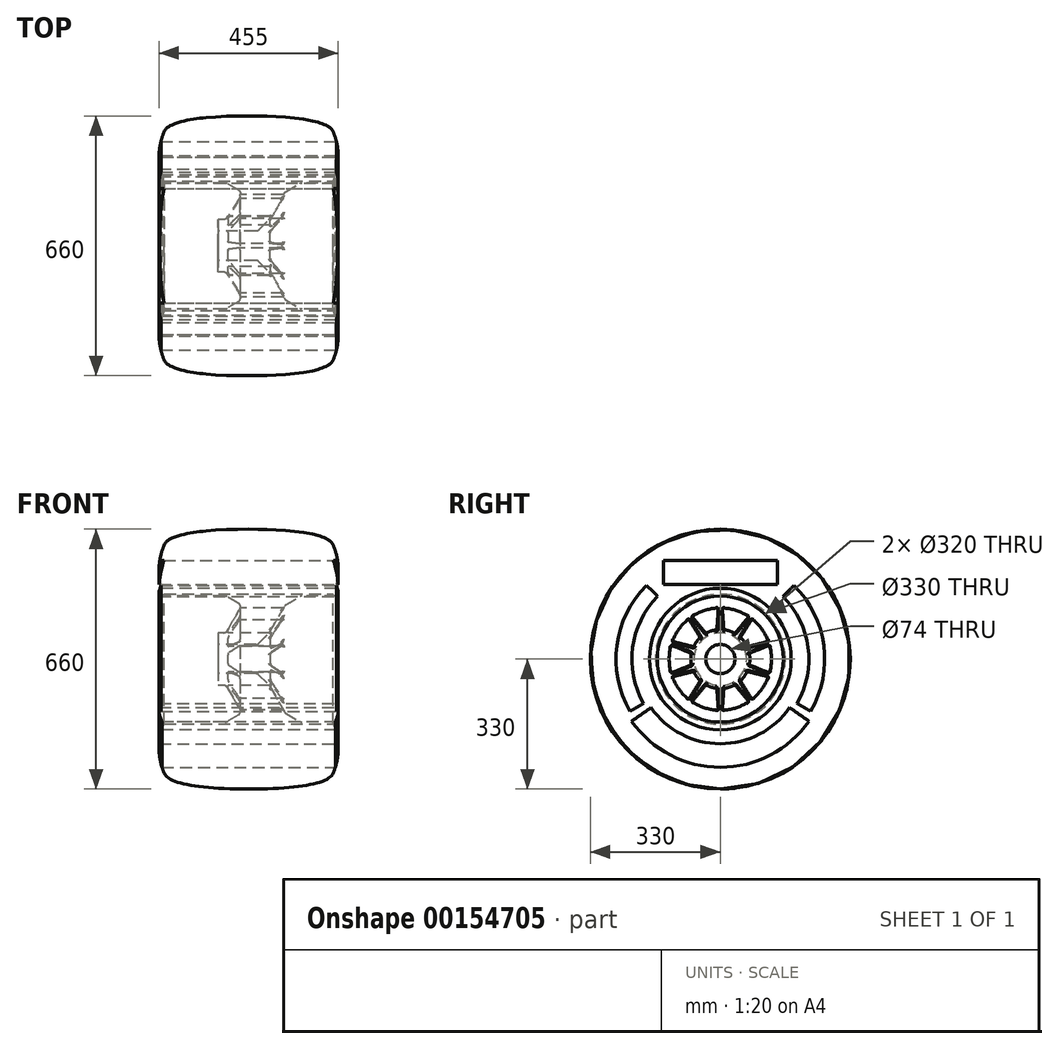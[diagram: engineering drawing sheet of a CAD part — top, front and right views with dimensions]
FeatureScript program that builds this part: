
annotation { "Feature Type Name" : "Feature", "Feature Type Description" : "" }
export const myFeature = defineFeature(function(context is Context, id is Id, definition is map)
    precondition{}
    {
        {
            var Q0;
            Q0=qCreatedBy(makeId("Front.planeOp"),FACE);
            var sketch = newSketch(context, id + "F0", { "sketchPlane" : qUnion([Q0])});
            skLineSegment(sketch, "E0.bottom", {"start": v(0, 0) * mm, "end": v(-232.5, 0) * mm, "construction": true});
            skLineSegment(sketch, "E0.top", {"start": v(0, 340) * mm, "end": v(-232.5, 340) * mm, "construction": true});
            skLineSegment(sketch, "E0.left", {"start": v(0, 0) * mm, "end": v(0, 340) * mm, "construction": true});
            skLineSegment(sketch, "E0.right", {"start": v(-232.5, 0) * mm, "end": v(-232.5, 340) * mm, "construction": true});
            skLineSegment(sketch, "E1", {"start": v(0, 165) * mm, "end": v(-214.65, 165) * mm});
            skEllipticalArc(sketch, "E2", {});
            skLineSegment(sketch, "E3", {"start": v(0, 330) * mm, "end": v(-232.5, 330) * mm, "construction": true});
            skLineSegment(sketch, "E4", {"start": v(-214.65, 165) * mm, "end": v(-214.65, 290) * mm, "construction": true});
            skEllipticalArc(sketch, "E5", {});
            skLineSegment(sketch, "E6", {"start": v(-227.5, 227.5) * mm, "end": v(-214.65, 227.5) * mm, "construction": true});
            skLineSegment(sketch, "E7.MirrorCS", {"start": v(0, 165) * mm, "end": v(214.65, 165) * mm});
            skEllipticalArc(sketch, "E8.MirrorCS", {});
            skEllipticalArc(sketch, "E9.MirrorCS", {});
            skLineSegment(sketch, "E10", {"start": v(-227.5, 227.5) * mm, "end": v(-227.5, 0) * mm, "construction": true});
            skLineSegment(sketch, "E11.MirrorCS", {"start": v(232.5, 0) * mm, "end": v(232.5, 340) * mm, "construction": true});
            skLineSegment(sketch, "E12.MirrorCS", {"start": v(0, 340) * mm, "end": v(232.5, 340) * mm, "construction": true});
            skLineSegment(sketch, "E13.MirrorCS", {"start": v(0, 0) * mm, "end": v(232.5, 0) * mm, "construction": true});
            const initialGuessF0  = {"E2": [0.9663548736200733, 0.07278752318222956, 0.9840924206940259, -0.17765727548449584, 1.201246100909484, 0.14589798289999634, 2.549372753708736, 3.1145633278998273], "E5": [0.08535, 0.2275, -1, 0, 0.31285, 0.22033704343395144, 5.995580380133269, 0.28760492704630874], "E8.MirrorCS": [-0.08535, 0.2275, 1, 0, 0.31285, 0.22033704343395144, 5.995580380133277, 0.28760492704631696], "E9.MirrorCS": [-0.9663548736200733, 0.07278752318222961, -0.984092420694026, -0.17765727548449584, 1.201246100909484, 0.14589798289999634, 3.168621979279758, 3.733812553470848]};
            skSetInitialGuess(sketch, initialGuessF0);
            skSolve(sketch);
        }
        {
            var Q0;
            Q0=qCreatedBy(makeId("Right.planeOp"),FACE);
            var sketch = newSketch(context, id + "F1", { "sketchPlane" : qUnion([Q0])});
            skLineSegment(sketch, "E14", {"start": v(0, 190) * mm, "end": v(0, -215) * mm, "construction": true});
            skLineSegment(sketch, "E15.bottom", {"start": v(0, 190) * mm, "end": v(-145, 190) * mm});
            skLineSegment(sketch, "E15.top", {"start": v(0, 250) * mm, "end": v(-145, 250) * mm});
            skLineSegment(sketch, "E15.left", {"start": v(0, 190) * mm, "end": v(0, 250) * mm});
            skLineSegment(sketch, "E15.right", {"start": v(-145, 190) * mm, "end": v(-145, 250) * mm});
            skArc(sketch, "E16", {"start": v(-159.1, 159.1) * mm, "mid": v(-223.08, 29.37) * mm, "end": v(-194.86, -112.5) * mm});
            skArc(sketch, "E17", {"start": v(-187.38, 187.38) * mm, "mid": v(-262.73, 34.59) * mm, "end": v(-229.5, -132.5) * mm});
            skLineSegment(sketch, "E18", {"start": v(-159.1, 159.1) * mm, "end": v(-187.38, 187.38) * mm});
            skLineSegment(sketch, "E19", {"start": v(-194.86, -112.5) * mm, "end": v(-229.5, -132.5) * mm});
            skArc(sketch, "E20", {"start": v(-176.12, -123.32) * mm, "mid": v(-99.28, -190.7) * mm, "end": v(0, -215) * mm});
            skArc(sketch, "E21", {"start": v(-225.27, -157.73) * mm, "mid": v(-126.98, -243.93) * mm, "end": v(0, -275) * mm});
            skLineSegment(sketch, "E22", {"start": v(-176.12, -123.32) * mm, "end": v(-225.27, -157.73) * mm});
            skLineSegment(sketch, "E23", {"start": v(0, -215) * mm, "end": v(0, -275) * mm});
            skLineSegment(sketch, "E24.MirrorCS", {"start": v(0, 250) * mm, "end": v(145, 250) * mm});
            skLineSegment(sketch, "E25.MirrorCS", {"start": v(145, 190) * mm, "end": v(145, 250) * mm});
            skLineSegment(sketch, "E26.MirrorCS", {"start": v(0, 190) * mm, "end": v(145, 190) * mm});
            skLineSegment(sketch, "E27.MirrorCS", {"start": v(159.1, 159.1) * mm, "end": v(187.38, 187.38) * mm});
            skArc(sketch, "E28.MirrorCS", {"start": v(187.38, 187.38) * mm, "mid": v(262.73, 34.59) * mm, "end": v(229.5, -132.5) * mm});
            skArc(sketch, "E29.MirrorCS", {"start": v(159.1, 159.1) * mm, "mid": v(223.08, 29.37) * mm, "end": v(194.86, -112.5) * mm});
            skLineSegment(sketch, "E30.MirrorCS", {"start": v(194.86, -112.5) * mm, "end": v(229.5, -132.5) * mm});
            skLineSegment(sketch, "E31.MirrorCS", {"start": v(176.12, -123.32) * mm, "end": v(225.27, -157.73) * mm});
            skArc(sketch, "E32.MirrorCS", {"start": v(225.27, -157.73) * mm, "mid": v(126.98, -243.93) * mm, "end": v(0, -275) * mm});
            skArc(sketch, "E33.MirrorCS", {"start": v(176.12, -123.32) * mm, "mid": v(99.28, -190.7) * mm, "end": v(0, -215) * mm});
            skSolve(sketch);
        }
        {
            var Q0;
            Q0=qCreatedBy(makeId("Front.planeOp"),FACE);
            var sketch = newSketch(context, id + "F2", { "sketchPlane" : qUnion([Q0])});
            skLineSegment(sketch, "E34.bottom", {"start": v(-222.5, 180) * mm, "end": v(222.5, 180) * mm});
            skLineSegment(sketch, "E34.top", {"start": v(-222.5, 160) * mm, "end": v(-60.18, 160) * mm});
            skLineSegment(sketch, "E34.left", {"start": v(-227.5, 175) * mm, "end": v(-227.5, 165) * mm});
            skLineSegment(sketch, "E34.right", {"start": v(227.5, 175) * mm, "end": v(227.5, 165) * mm});
            skPoint(sketch, "E35.visualSharp", {"position": v(-227.5, 160) * mm});
            skArc(sketch, "E35.filletArc", {"start": v(-227.5, 165) * mm, "mid": v(-226.04, 161.46) * mm, "end": v(-222.5, 160) * mm});
            skPoint(sketch, "E36.visualSharp", {"position": v(227.5, 160) * mm});
            skArc(sketch, "E36.filletArc", {"start": v(222.5, 160) * mm, "mid": v(226.04, 161.46) * mm, "end": v(227.5, 165) * mm});
            skPoint(sketch, "E37.visualSharp", {"position": v(227.5, 180) * mm});
            skArc(sketch, "E37.filletArc", {"start": v(227.5, 175) * mm, "mid": v(226.04, 178.54) * mm, "end": v(222.5, 180) * mm});
            skPoint(sketch, "E38.visualSharp", {"position": v(-227.5, 180) * mm});
            skArc(sketch, "E38.filletArc", {"start": v(-222.5, 180) * mm, "mid": v(-226.04, 178.54) * mm, "end": v(-227.5, 175) * mm});
            skLineSegment(sketch, "E39", {"start": v(18.36, 37) * mm, "end": v(-77.5, 37) * mm});
            skLineSegment(sketch, "E40", {"start": v(-77.5, 37) * mm, "end": v(-77.5, 67) * mm});
            skLineSegment(sketch, "E41", {"start": v(-77.5, 67) * mm, "end": v(-63.27, 67) * mm});
            skLineSegment(sketch, "E42", {"start": v(-54.61, 72) * mm, "end": v(-22.23, 128.09) * mm});
            skLineSegment(sketch, "E43", {"start": v(-25.9, 141.75) * mm, "end": v(-55.18, 158.66) * mm});
            skLineSegment(sketch, "E44", {"start": v(25.43, 39.93) * mm, "end": v(51.57, 66.07) * mm});
            skLineSegment(sketch, "E45", {"start": v(53.16, 68.14) * mm, "end": v(91.43, 134.43) * mm});
            skLineSegment(sketch, "E46", {"start": v(95.1, 138.09) * mm, "end": v(130.72, 158.66) * mm});
            skLineSegment(sketch, "E47.trimOffspring", {"start": v(135.72, 160) * mm, "end": v(222.5, 160) * mm});
            skPoint(sketch, "E48.visualSharp", {"position": v(-57.5, 160) * mm});
            skArc(sketch, "E48.filletArc", {"start": v(-55.18, 158.66) * mm, "mid": v(-57.6, 159.66) * mm, "end": v(-60.18, 160) * mm});
            skPoint(sketch, "E49.visualSharp", {"position": v(-57.5, 67) * mm});
            skArc(sketch, "E49.filletArc", {"start": v(-63.27, 67) * mm, "mid": v(-58.27, 68.34) * mm, "end": v(-54.61, 72) * mm});
            skPoint(sketch, "E50.visualSharp", {"position": v(22.5, 37) * mm});
            skArc(sketch, "E50.filletArc", {"start": v(18.36, 37) * mm, "mid": v(22.18, 37.76) * mm, "end": v(25.43, 39.93) * mm});
            skPoint(sketch, "E51.visualSharp", {"position": v(52.5, 67) * mm});
            skArc(sketch, "E51.filletArc", {"start": v(51.57, 66.07) * mm, "mid": v(52.43, 67.05) * mm, "end": v(53.16, 68.14) * mm});
            skPoint(sketch, "E52.visualSharp", {"position": v(92.77, 136.75) * mm});
            skPoint(sketch, "E53.visualSharp", {"position": v(133.04, 160) * mm});
            skArc(sketch, "E53.filletArc", {"start": v(135.72, 160) * mm, "mid": v(133.13, 159.66) * mm, "end": v(130.72, 158.66) * mm});
            skPoint(sketch, "E54.visualSharp", {"position": v(-17.23, 136.75) * mm});
            skArc(sketch, "E54.filletArc", {"start": v(-22.23, 128.09) * mm, "mid": v(-21.23, 135.68) * mm, "end": v(-25.9, 141.75) * mm});
            skArc(sketch, "E55.filletArc", {"start": v(95.1, 138.09) * mm, "mid": v(93.02, 136.5) * mm, "end": v(91.43, 134.43) * mm});
            skSolve(sketch);
        }
        {
            var Q0;
            Q0=qCreatedBy(makeId("Right.planeOp"),FACE);
            var sketch = newSketch(context, id + "F3", { "sketchPlane" : qUnion([Q0])});
            skLineSegment(sketch, "E56", {"start": v(5.4, 124.22) * mm, "end": v(8.6, 78.49) * mm});
            skLineSegment(sketch, "E57", {"start": v(40.17, 123.64) * mm, "end": v(23.18, 71.33) * mm, "construction": true});
            skLineSegment(sketch, "E58", {"start": v(23.18, 71.33) * mm, "end": v(0, 0) * mm, "construction": true});
            skArc(sketch, "E59", {"start": v(23.18, 71.33) * mm, "mid": v(18, 72.8) * mm, "end": v(12.73, 73.91) * mm});
            skArc(sketch, "E60", {"start": v(40.17, 123.64) * mm, "mid": v(25.66, 127.44) * mm, "end": v(10.8, 129.55) * mm});
            skArc(sketch, "E61.MirrorCS", {"start": v(23.18, 71.33) * mm, "mid": v(28.23, 69.48) * mm, "end": v(33.14, 67.28) * mm});
            skLineSegment(sketch, "E62.MirrorCS", {"start": v(68.65, 103.67) * mm, "end": v(39.18, 68.55) * mm});
            skArc(sketch, "E63.MirrorCS", {"start": v(40.17, 123.64) * mm, "mid": v(54.15, 118.18) * mm, "end": v(67.4, 111.16) * mm});
            skPoint(sketch, "E64.visualSharp", {"position": v(8.88, 74.47) * mm});
            skArc(sketch, "E64.filletArc", {"start": v(8.6, 78.49) * mm, "mid": v(9.87, 75.49) * mm, "end": v(12.73, 73.91) * mm});
            skPoint(sketch, "E65.visualSharp", {"position": v(5, 129.9) * mm});
            skArc(sketch, "E65.filletArc", {"start": v(10.8, 129.55) * mm, "mid": v(6.87, 128.13) * mm, "end": v(5.4, 124.22) * mm});
            skPoint(sketch, "E66.visualSharp", {"position": v(36.6, 65.47) * mm});
            skArc(sketch, "E66.filletArc", {"start": v(33.14, 67.28) * mm, "mid": v(36.38, 66.87) * mm, "end": v(39.18, 68.55) * mm});
            skPoint(sketch, "E67.visualSharp", {"position": v(72.31, 108.03) * mm});
            skArc(sketch, "E67.filletArc", {"start": v(68.65, 103.67) * mm, "mid": v(69.75, 107.7) * mm, "end": v(67.4, 111.16) * mm});
            skLineSegment(sketch, "E68.1.0", {"start": v(-5.4, 124.22) * mm, "end": v(-8.6, 78.49) * mm});
            skArc(sketch, "E68.1.1", {"start": v(-5.4, 124.22) * mm, "mid": v(-6.87, 128.13) * mm, "end": v(-10.8, 129.55) * mm});
            skArc(sketch, "E68.1.2", {"start": v(-40.17, 123.64) * mm, "mid": v(-25.66, 127.44) * mm, "end": v(-10.8, 129.55) * mm});
            skArc(sketch, "E68.1.3", {"start": v(-40.17, 123.64) * mm, "mid": v(-54.15, 118.18) * mm, "end": v(-67.4, 111.16) * mm});
            skArc(sketch, "E68.1.4", {"start": v(-67.4, 111.16) * mm, "mid": v(-69.75, 107.7) * mm, "end": v(-68.65, 103.67) * mm});
            skLineSegment(sketch, "E68.1.5", {"start": v(-68.65, 103.67) * mm, "end": v(-39.18, 68.55) * mm});
            skArc(sketch, "E68.1.6", {"start": v(-39.18, 68.55) * mm, "mid": v(-36.38, 66.87) * mm, "end": v(-33.14, 67.28) * mm});
            skArc(sketch, "E68.1.7", {"start": v(-23.18, 71.33) * mm, "mid": v(-28.23, 69.48) * mm, "end": v(-33.14, 67.28) * mm});
            skArc(sketch, "E68.1.8", {"start": v(-23.18, 71.33) * mm, "mid": v(-18, 72.8) * mm, "end": v(-12.73, 73.91) * mm});
            skArc(sketch, "E68.1.9", {"start": v(-12.73, 73.91) * mm, "mid": v(-9.87, 75.49) * mm, "end": v(-8.6, 78.49) * mm});
            skLineSegment(sketch, "E68.2.0", {"start": v(-77.38, 97.32) * mm, "end": v(-53.09, 58.45) * mm});
            skArc(sketch, "E68.2.1", {"start": v(-77.38, 97.32) * mm, "mid": v(-80.87, 99.62) * mm, "end": v(-84.89, 98.46) * mm});
            skArc(sketch, "E68.2.2", {"start": v(-105.17, 76.41) * mm, "mid": v(-95.67, 88.02) * mm, "end": v(-84.89, 98.46) * mm});
            skArc(sketch, "E68.2.3", {"start": v(-105.17, 76.41) * mm, "mid": v(-113.28, 63.78) * mm, "end": v(-119.87, 50.3) * mm});
            skArc(sketch, "E68.2.4", {"start": v(-119.87, 50.3) * mm, "mid": v(-119.73, 46.13) * mm, "end": v(-116.47, 43.52) * mm});
            skLineSegment(sketch, "E68.2.5", {"start": v(-116.47, 43.52) * mm, "end": v(-72, 32.43) * mm});
            skArc(sketch, "E68.2.6", {"start": v(-72, 32.43) * mm, "mid": v(-68.74, 32.72) * mm, "end": v(-66.36, 34.95) * mm});
            skArc(sketch, "E68.2.7", {"start": v(-60.68, 44.08) * mm, "mid": v(-63.68, 39.62) * mm, "end": v(-66.36, 34.95) * mm});
            skArc(sketch, "E68.2.8", {"start": v(-60.68, 44.08) * mm, "mid": v(-57.36, 48.32) * mm, "end": v(-53.75, 52.31) * mm});
            skArc(sketch, "E68.2.9", {"start": v(-53.75, 52.31) * mm, "mid": v(-52.36, 55.27) * mm, "end": v(-53.09, 58.45) * mm});
            skLineSegment(sketch, "E68.3.0", {"start": v(-119.8, 33.25) * mm, "end": v(-77.3, 16.08) * mm});
            skArc(sketch, "E68.3.1", {"start": v(-119.8, 33.25) * mm, "mid": v(-123.98, 33.06) * mm, "end": v(-126.55, 29.76) * mm});
            skArc(sketch, "E68.3.2", {"start": v(-130, 0) * mm, "mid": v(-129.13, 14.98) * mm, "end": v(-126.55, 29.76) * mm});
            skArc(sketch, "E68.3.3", {"start": v(-130, 0) * mm, "mid": v(-129.13, -14.98) * mm, "end": v(-126.55, -29.76) * mm});
            skArc(sketch, "E68.3.4", {"start": v(-126.55, -29.76) * mm, "mid": v(-123.98, -33.06) * mm, "end": v(-119.8, -33.25) * mm});
            skLineSegment(sketch, "E68.3.5", {"start": v(-119.8, -33.25) * mm, "end": v(-77.3, -16.08) * mm});
            skArc(sketch, "E68.3.6", {"start": v(-77.3, -16.08) * mm, "mid": v(-74.84, -13.94) * mm, "end": v(-74.23, -10.73) * mm});
            skArc(sketch, "E68.3.7", {"start": v(-75, 0) * mm, "mid": v(-74.8, -5.38) * mm, "end": v(-74.23, -10.73) * mm});
            skArc(sketch, "E68.3.8", {"start": v(-75, 0) * mm, "mid": v(-74.8, 5.38) * mm, "end": v(-74.23, 10.73) * mm});
            skArc(sketch, "E68.3.9", {"start": v(-74.23, 10.73) * mm, "mid": v(-74.84, 13.94) * mm, "end": v(-77.3, 16.08) * mm});
            skLineSegment(sketch, "E68.4.0", {"start": v(-116.47, -43.52) * mm, "end": v(-72, -32.43) * mm});
            skArc(sketch, "E68.4.1", {"start": v(-116.47, -43.52) * mm, "mid": v(-119.73, -46.13) * mm, "end": v(-119.87, -50.3) * mm});
            skArc(sketch, "E68.4.2", {"start": v(-105.17, -76.41) * mm, "mid": v(-113.28, -63.78) * mm, "end": v(-119.87, -50.3) * mm});
            skArc(sketch, "E68.4.3", {"start": v(-105.17, -76.41) * mm, "mid": v(-95.67, -88.02) * mm, "end": v(-84.89, -98.46) * mm});
            skArc(sketch, "E68.4.4", {"start": v(-84.89, -98.46) * mm, "mid": v(-80.87, -99.62) * mm, "end": v(-77.38, -97.32) * mm});
            skLineSegment(sketch, "E68.4.5", {"start": v(-77.38, -97.32) * mm, "end": v(-53.09, -58.45) * mm});
            skArc(sketch, "E68.4.6", {"start": v(-53.09, -58.45) * mm, "mid": v(-52.36, -55.27) * mm, "end": v(-53.75, -52.31) * mm});
            skArc(sketch, "E68.4.7", {"start": v(-60.68, -44.08) * mm, "mid": v(-57.36, -48.32) * mm, "end": v(-53.75, -52.31) * mm});
            skArc(sketch, "E68.4.8", {"start": v(-60.68, -44.08) * mm, "mid": v(-63.68, -39.62) * mm, "end": v(-66.36, -34.95) * mm});
            skArc(sketch, "E68.4.9", {"start": v(-66.36, -34.95) * mm, "mid": v(-68.74, -32.72) * mm, "end": v(-72, -32.43) * mm});
            skLineSegment(sketch, "E68.5.0", {"start": v(-68.65, -103.67) * mm, "end": v(-39.18, -68.55) * mm});
            skArc(sketch, "E68.5.1", {"start": v(-68.65, -103.67) * mm, "mid": v(-69.75, -107.7) * mm, "end": v(-67.4, -111.16) * mm});
            skArc(sketch, "E68.5.2", {"start": v(-40.17, -123.64) * mm, "mid": v(-54.15, -118.18) * mm, "end": v(-67.4, -111.16) * mm});
            skArc(sketch, "E68.5.3", {"start": v(-40.17, -123.64) * mm, "mid": v(-25.66, -127.44) * mm, "end": v(-10.8, -129.55) * mm});
            skArc(sketch, "E68.5.4", {"start": v(-10.8, -129.55) * mm, "mid": v(-6.87, -128.13) * mm, "end": v(-5.4, -124.22) * mm});
            skLineSegment(sketch, "E68.5.5", {"start": v(-5.4, -124.22) * mm, "end": v(-8.6, -78.49) * mm});
            skArc(sketch, "E68.5.6", {"start": v(-8.6, -78.49) * mm, "mid": v(-9.87, -75.49) * mm, "end": v(-12.73, -73.91) * mm});
            skArc(sketch, "E68.5.7", {"start": v(-23.18, -71.33) * mm, "mid": v(-18, -72.8) * mm, "end": v(-12.73, -73.91) * mm});
            skArc(sketch, "E68.5.8", {"start": v(-23.18, -71.33) * mm, "mid": v(-28.23, -69.48) * mm, "end": v(-33.14, -67.28) * mm});
            skArc(sketch, "E68.5.9", {"start": v(-33.14, -67.28) * mm, "mid": v(-36.38, -66.87) * mm, "end": v(-39.18, -68.55) * mm});
            skLineSegment(sketch, "E68.6.0", {"start": v(5.4, -124.22) * mm, "end": v(8.6, -78.49) * mm});
            skArc(sketch, "E68.6.1", {"start": v(5.4, -124.22) * mm, "mid": v(6.87, -128.13) * mm, "end": v(10.8, -129.55) * mm});
            skArc(sketch, "E68.6.2", {"start": v(40.17, -123.64) * mm, "mid": v(25.66, -127.44) * mm, "end": v(10.8, -129.55) * mm});
            skArc(sketch, "E68.6.3", {"start": v(40.17, -123.64) * mm, "mid": v(54.15, -118.18) * mm, "end": v(67.4, -111.16) * mm});
            skArc(sketch, "E68.6.4", {"start": v(67.4, -111.16) * mm, "mid": v(69.75, -107.7) * mm, "end": v(68.65, -103.67) * mm});
            skLineSegment(sketch, "E68.6.5", {"start": v(68.65, -103.67) * mm, "end": v(39.18, -68.55) * mm});
            skArc(sketch, "E68.6.6", {"start": v(39.18, -68.55) * mm, "mid": v(36.38, -66.87) * mm, "end": v(33.14, -67.28) * mm});
            skArc(sketch, "E68.6.7", {"start": v(23.18, -71.33) * mm, "mid": v(28.23, -69.48) * mm, "end": v(33.14, -67.28) * mm});
            skArc(sketch, "E68.6.8", {"start": v(23.18, -71.33) * mm, "mid": v(18, -72.8) * mm, "end": v(12.73, -73.91) * mm});
            skArc(sketch, "E68.6.9", {"start": v(12.73, -73.91) * mm, "mid": v(9.87, -75.49) * mm, "end": v(8.6, -78.49) * mm});
            skLineSegment(sketch, "E68.7.0", {"start": v(77.38, -97.32) * mm, "end": v(53.09, -58.45) * mm});
            skArc(sketch, "E68.7.1", {"start": v(77.38, -97.32) * mm, "mid": v(80.87, -99.62) * mm, "end": v(84.89, -98.46) * mm});
            skArc(sketch, "E68.7.2", {"start": v(105.17, -76.41) * mm, "mid": v(95.67, -88.02) * mm, "end": v(84.89, -98.46) * mm});
            skArc(sketch, "E68.7.3", {"start": v(105.17, -76.41) * mm, "mid": v(113.28, -63.78) * mm, "end": v(119.87, -50.3) * mm});
            skArc(sketch, "E68.7.4", {"start": v(119.87, -50.3) * mm, "mid": v(119.73, -46.13) * mm, "end": v(116.47, -43.52) * mm});
            skLineSegment(sketch, "E68.7.5", {"start": v(116.47, -43.52) * mm, "end": v(72, -32.43) * mm});
            skArc(sketch, "E68.7.6", {"start": v(72, -32.43) * mm, "mid": v(68.74, -32.72) * mm, "end": v(66.36, -34.95) * mm});
            skArc(sketch, "E68.7.7", {"start": v(60.68, -44.08) * mm, "mid": v(63.68, -39.62) * mm, "end": v(66.36, -34.95) * mm});
            skArc(sketch, "E68.7.8", {"start": v(60.68, -44.08) * mm, "mid": v(57.36, -48.32) * mm, "end": v(53.75, -52.31) * mm});
            skArc(sketch, "E68.7.9", {"start": v(53.75, -52.31) * mm, "mid": v(52.36, -55.27) * mm, "end": v(53.09, -58.45) * mm});
            skLineSegment(sketch, "E68.8.0", {"start": v(119.8, -33.25) * mm, "end": v(77.3, -16.08) * mm});
            skArc(sketch, "E68.8.1", {"start": v(119.8, -33.25) * mm, "mid": v(123.98, -33.06) * mm, "end": v(126.55, -29.76) * mm});
            skArc(sketch, "E68.8.2", {"start": v(130, 0) * mm, "mid": v(129.13, -14.98) * mm, "end": v(126.55, -29.76) * mm});
            skArc(sketch, "E68.8.3", {"start": v(130, 0) * mm, "mid": v(129.13, 14.98) * mm, "end": v(126.55, 29.76) * mm});
            skArc(sketch, "E68.8.4", {"start": v(126.55, 29.76) * mm, "mid": v(123.98, 33.06) * mm, "end": v(119.8, 33.25) * mm});
            skLineSegment(sketch, "E68.8.5", {"start": v(119.8, 33.25) * mm, "end": v(77.3, 16.08) * mm});
            skArc(sketch, "E68.8.6", {"start": v(77.3, 16.08) * mm, "mid": v(74.84, 13.94) * mm, "end": v(74.23, 10.73) * mm});
            skArc(sketch, "E68.8.7", {"start": v(75, 0) * mm, "mid": v(74.8, 5.38) * mm, "end": v(74.23, 10.73) * mm});
            skArc(sketch, "E68.8.8", {"start": v(75, 0) * mm, "mid": v(74.8, -5.38) * mm, "end": v(74.23, -10.73) * mm});
            skArc(sketch, "E68.8.9", {"start": v(74.23, -10.73) * mm, "mid": v(74.84, -13.94) * mm, "end": v(77.3, -16.08) * mm});
            skLineSegment(sketch, "E68.9.0", {"start": v(116.47, 43.52) * mm, "end": v(72, 32.43) * mm});
            skArc(sketch, "E68.9.1", {"start": v(116.47, 43.52) * mm, "mid": v(119.73, 46.13) * mm, "end": v(119.87, 50.3) * mm});
            skArc(sketch, "E68.9.2", {"start": v(105.17, 76.41) * mm, "mid": v(113.28, 63.78) * mm, "end": v(119.87, 50.3) * mm});
            skArc(sketch, "E68.9.3", {"start": v(105.17, 76.41) * mm, "mid": v(95.67, 88.02) * mm, "end": v(84.89, 98.46) * mm});
            skArc(sketch, "E68.9.4", {"start": v(84.89, 98.46) * mm, "mid": v(80.87, 99.62) * mm, "end": v(77.38, 97.32) * mm});
            skLineSegment(sketch, "E68.9.5", {"start": v(77.38, 97.32) * mm, "end": v(53.09, 58.45) * mm});
            skArc(sketch, "E68.9.6", {"start": v(53.09, 58.45) * mm, "mid": v(52.36, 55.27) * mm, "end": v(53.75, 52.31) * mm});
            skArc(sketch, "E68.9.7", {"start": v(60.68, 44.08) * mm, "mid": v(57.36, 48.32) * mm, "end": v(53.75, 52.31) * mm});
            skArc(sketch, "E68.9.8", {"start": v(60.68, 44.08) * mm, "mid": v(63.68, 39.62) * mm, "end": v(66.36, 34.95) * mm});
            skArc(sketch, "E68.9.9", {"start": v(66.36, 34.95) * mm, "mid": v(68.74, 32.72) * mm, "end": v(72, 32.43) * mm});
            skSolve(sketch);
        }
        {
            var Q0;
            Q0=makeQuery(id+"F0.imprint","IMPRINT",FACE,{"disambiguationData":[TD([[makeQuery(id+"F0.imprint","IMPRINT",EDGE,{"derivedFrom":sQuery(id+"F0.wireOp",EDGE,"E1")}),-1.0]])]});
            var Q1;
            Q1=sQuery(id+"F0.wireOp",EDGE,"E0.bottom");
            revolve(context, id + "F4", {"entities" : qUnion([Q0]), "axis" : qUnion([Q1]), "revolveType" : RevolveType.FULL});
        }
        {
            var Q0;
            Q0=qSketchRegion(id+"F1",true);
            var Q1;
            Q1=makeQuery(id+"F4.opRevolve","SWEPT_FACE",FACE,{"disambiguationData":[OSD([sQuery(id+"F0.wireOp",EDGE,"E5")])]});
            extrude(context, id + "F5", {"entities" : qUnion([Q0]), "endBound" : BoundingType.UP_TO_NEXT, "oppositeDirection" : true, "depth" : 25 * mm, "hasSecondDirection" : true, "secondDirectionBound" : SecondDirectionBoundingType.UP_TO_NEXT, "secondDirectionOppositeDirection" : false, "secondDirectionBoundEntityFace" : qUnion([Q1]), "secondDirectionDepth" : 25 * mm});
        }
        {
            var Q0;
            Q0=makeQuery(id+"F5.opExtrude","SWEPT_BODY",BODY,{"disambiguationData":[OSD([sQuery(id+"F1.wireOp",EDGE,"E15.bottom"),sQuery(id+"F1.wireOp",EDGE,"E15.top"),sQuery(id+"F1.wireOp",EDGE,"E15.right"),sQuery(id+"F1.wireOp",EDGE,"E24.MirrorCS"),sQuery(id+"F1.wireOp",EDGE,"E25.MirrorCS"),sQuery(id+"F1.wireOp",EDGE,"E26.MirrorCS")])]});
            var Q1;
            Q1=makeQuery(id+"F5.opExtrude","SWEPT_BODY",BODY,{"disambiguationData":[OSD([sQuery(id+"F1.wireOp",EDGE,"E27.MirrorCS"),sQuery(id+"F1.wireOp",EDGE,"E28.MirrorCS"),sQuery(id+"F1.wireOp",EDGE,"E29.MirrorCS"),sQuery(id+"F1.wireOp",EDGE,"E30.MirrorCS")])]});
            var Q2;
            Q2=makeQuery(id+"F5.opExtrude","SWEPT_BODY",BODY,{"disambiguationData":[OSD([sQuery(id+"F1.wireOp",EDGE,"E20"),sQuery(id+"F1.wireOp",EDGE,"E21"),sQuery(id+"F1.wireOp",EDGE,"E22"),sQuery(id+"F1.wireOp",EDGE,"E31.MirrorCS"),sQuery(id+"F1.wireOp",EDGE,"E32.MirrorCS"),sQuery(id+"F1.wireOp",EDGE,"E33.MirrorCS")])]});
            var Q3;
            Q3=makeQuery(id+"F5.opExtrude","SWEPT_BODY",BODY,{"disambiguationData":[OSD([sQuery(id+"F1.wireOp",EDGE,"E16"),sQuery(id+"F1.wireOp",EDGE,"E17"),sQuery(id+"F1.wireOp",EDGE,"E18"),sQuery(id+"F1.wireOp",EDGE,"E19")])]});
            var Q4;
            Q4=makeQuery(id+"F4.opRevolve","SWEPT_BODY",BODY,{"disambiguationData":[OSD([sQuery(id+"F0.wireOp",EDGE,"E1"),sQuery(id+"F0.wireOp",EDGE,"E2"),sQuery(id+"F0.wireOp",EDGE,"E5"),sQuery(id+"F0.wireOp",EDGE,"E7.MirrorCS"),sQuery(id+"F0.wireOp",EDGE,"E8.MirrorCS"),sQuery(id+"F0.wireOp",EDGE,"E9.MirrorCS")])]});
            booleanBodies(context, id + "F6", {"operationType" : BooleanOperationType.SUBTRACTION, "tools" : qUnion([Q0, Q1, Q2, Q3]), "targets" : qUnion([Q4]), "keepTools" : true});
        }
        {
            var Q0;
            Q0=qSketchRegion(id+"F2",true);
            var Q1;
            Q1=sQuery(id+"F0.wireOp",EDGE,"E13.MirrorCS");
            revolve(context, id + "F7", {"entities" : qUnion([Q0]), "axis" : qUnion([Q1]), "revolveType" : RevolveType.FULL});
        }
        {
            var Q0;
            Q0=qSketchRegion(id+"F3",true);
            extrude(context, id + "F8", {"entities" : qUnion([Q0]), "operationType" : NewBodyOperationType.REMOVE, "endBound" : BoundingType.THROUGH_ALL, "depth" : 25 * mm, "hasSecondDirection" : true, "secondDirectionBound" : SecondDirectionBoundingType.THROUGH_ALL, "secondDirectionOppositeDirection" : true, "secondDirectionDepth" : 25 * mm});
        }
        {
            var Q0;
            Q0=makeQuery(id+"F8.boolean.opBoolean","INTERSECT",EDGE,{"derivedFrom":[makeQuery(id+"F7.opRevolve","SWEPT_FACE",FACE,{"disambiguationData":[OSD([sQuery(id+"F2.wireOp",EDGE,"E45")])]}),makeQuery(id+"F8.opExtrude","SWEPT_FACE",FACE,{"disambiguationData":[OSD([sQuery(id+"F3.wireOp",EDGE,"E68.1.5")])]})]});
            var Q1;
            Q1=makeQuery(id+"F8.boolean.opBoolean","INTERSECT",EDGE,{"derivedFrom":[makeQuery(id+"F7.opRevolve","SWEPT_FACE",FACE,{"disambiguationData":[OSD([sQuery(id+"F2.wireOp",EDGE,"E45")])]}),makeQuery(id+"F8.opExtrude","SWEPT_FACE",FACE,{"disambiguationData":[OSD([sQuery(id+"F3.wireOp",EDGE,"E56")])]})]});
            var Q2;
            Q2=makeQuery(id+"F8.boolean.opBoolean","INTERSECT",EDGE,{"derivedFrom":[makeQuery(id+"F7.opRevolve","SWEPT_FACE",FACE,{"disambiguationData":[OSD([sQuery(id+"F2.wireOp",EDGE,"E45")])]}),makeQuery(id+"F8.opExtrude","SWEPT_FACE",FACE,{"disambiguationData":[OSD([sQuery(id+"F3.wireOp",EDGE,"E68.9.5")])]})]});
            var Q3;
            Q3=makeQuery(id+"F8.boolean.opBoolean","INTERSECT",EDGE,{"derivedFrom":[makeQuery(id+"F7.opRevolve","SWEPT_FACE",FACE,{"disambiguationData":[OSD([sQuery(id+"F2.wireOp",EDGE,"E45")])]}),makeQuery(id+"F8.opExtrude","SWEPT_FACE",FACE,{"disambiguationData":[OSD([sQuery(id+"F3.wireOp",EDGE,"E68.8.5")])]})]});
            var Q4;
            Q4=makeQuery(id+"F8.boolean.opBoolean","INTERSECT",EDGE,{"derivedFrom":[makeQuery(id+"F7.opRevolve","SWEPT_FACE",FACE,{"disambiguationData":[OSD([sQuery(id+"F2.wireOp",EDGE,"E45")])]}),makeQuery(id+"F8.opExtrude","SWEPT_FACE",FACE,{"disambiguationData":[OSD([sQuery(id+"F3.wireOp",EDGE,"E68.7.5")])]})]});
            var Q5;
            Q5=makeQuery(id+"F8.boolean.opBoolean","INTERSECT",EDGE,{"derivedFrom":[makeQuery(id+"F7.opRevolve","SWEPT_FACE",FACE,{"disambiguationData":[OSD([sQuery(id+"F2.wireOp",EDGE,"E45")])]}),makeQuery(id+"F8.opExtrude","SWEPT_FACE",FACE,{"disambiguationData":[OSD([sQuery(id+"F3.wireOp",EDGE,"E68.6.5")])]})]});
            var Q6;
            Q6=makeQuery(id+"F8.boolean.opBoolean","INTERSECT",EDGE,{"derivedFrom":[makeQuery(id+"F7.opRevolve","SWEPT_FACE",FACE,{"disambiguationData":[OSD([sQuery(id+"F2.wireOp",EDGE,"E45")])]}),makeQuery(id+"F8.opExtrude","SWEPT_FACE",FACE,{"disambiguationData":[OSD([sQuery(id+"F3.wireOp",EDGE,"E68.5.5")])]})]});
            var Q7;
            Q7=makeQuery(id+"F8.boolean.opBoolean","INTERSECT",EDGE,{"derivedFrom":[makeQuery(id+"F7.opRevolve","SWEPT_FACE",FACE,{"disambiguationData":[OSD([sQuery(id+"F2.wireOp",EDGE,"E45")])]}),makeQuery(id+"F8.opExtrude","SWEPT_FACE",FACE,{"disambiguationData":[OSD([sQuery(id+"F3.wireOp",EDGE,"E68.4.5")])]})]});
            var Q8;
            Q8=makeQuery(id+"F8.boolean.opBoolean","INTERSECT",EDGE,{"derivedFrom":[makeQuery(id+"F7.opRevolve","SWEPT_FACE",FACE,{"disambiguationData":[OSD([sQuery(id+"F2.wireOp",EDGE,"E45")])]}),makeQuery(id+"F8.opExtrude","SWEPT_FACE",FACE,{"disambiguationData":[OSD([sQuery(id+"F3.wireOp",EDGE,"E68.3.5")])]})]});
            var Q9;
            Q9=makeQuery(id+"F8.boolean.opBoolean","INTERSECT",EDGE,{"derivedFrom":[makeQuery(id+"F7.opRevolve","SWEPT_FACE",FACE,{"disambiguationData":[OSD([sQuery(id+"F2.wireOp",EDGE,"E45")])]}),makeQuery(id+"F8.opExtrude","SWEPT_FACE",FACE,{"disambiguationData":[OSD([sQuery(id+"F3.wireOp",EDGE,"E68.2.5")])]})]});
            fillet(context, id + "F9", {"entities" : qUnion([Q0, Q1, Q2, Q3, Q4, Q5, Q6, Q7, Q8, Q9]), "radius" : 3 * mm, "tangentPropagation" : true, "allowEdgeOverflow" : false});
        }
    });
